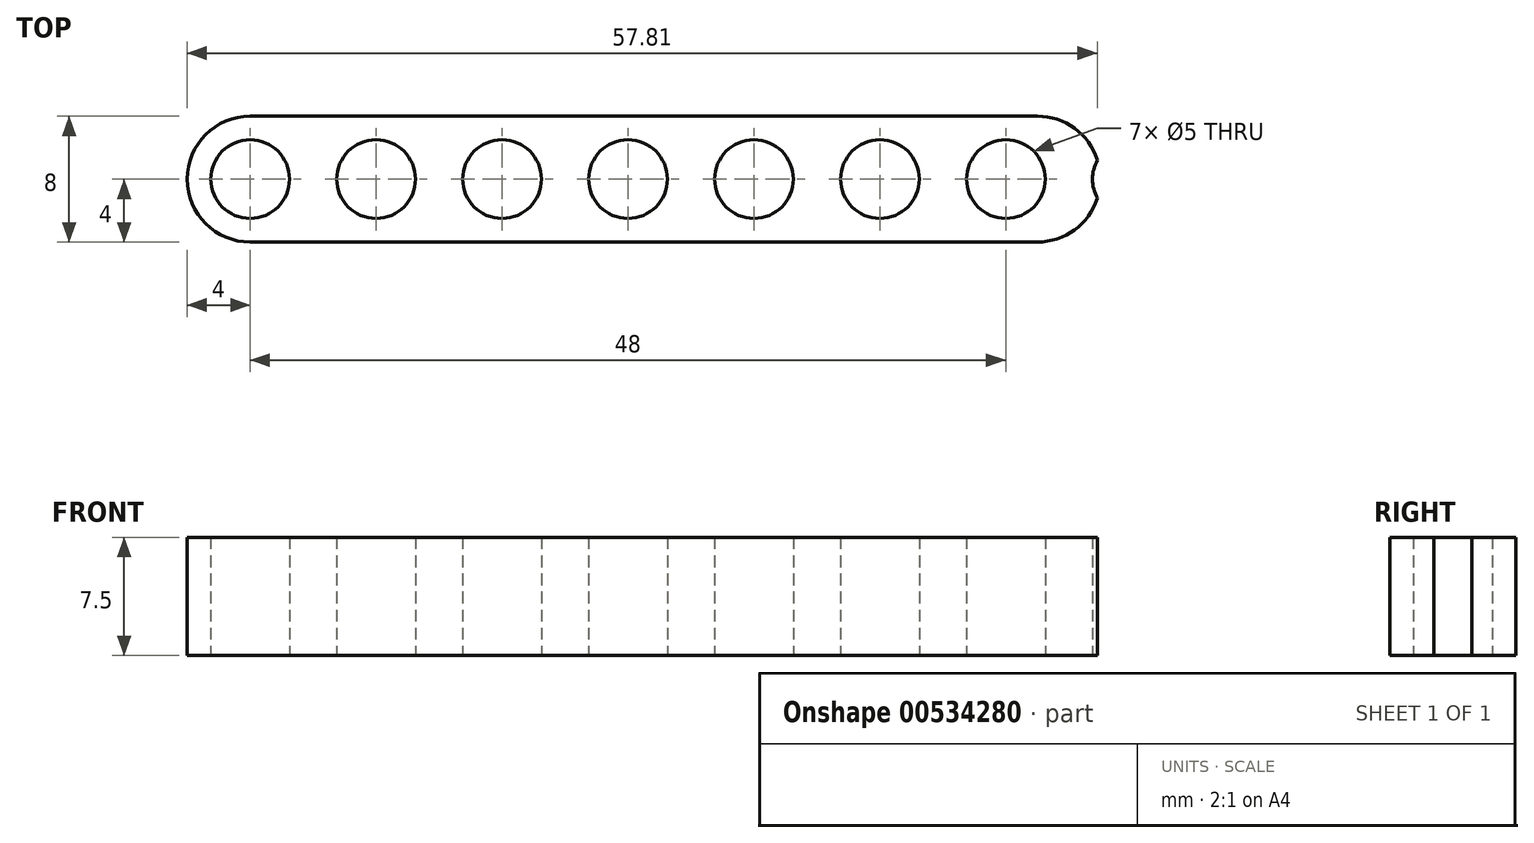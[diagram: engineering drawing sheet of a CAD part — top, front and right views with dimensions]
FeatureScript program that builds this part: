
annotation { "Feature Type Name" : "Feature", "Feature Type Description" : "" }
export const myFeature = defineFeature(function(context is Context, id is Id, definition is map)
    precondition{}
    {
        {
            var Q0;
            Q0=qCreatedBy(makeId("Top.planeOp"),FACE);
            var sketch = newSketch(context, id + "F0", { "sketchPlane" : qUnion([Q0])});
            skCircle(sketch, "E0", {"center": v(0, 0) * mm, "radius": 2.5 * mm});
            skCircle(sketch, "E1.1.0.0", {"center": v(8, 0) * mm, "radius": 2.5 * mm});
            skCircle(sketch, "E1.2.0.0", {"center": v(16, 0) * mm, "radius": 2.5 * mm});
            skCircle(sketch, "E1.3.0.0", {"center": v(24, 0) * mm, "radius": 2.5 * mm});
            skCircle(sketch, "E1.4.0.0", {"center": v(32, 0) * mm, "radius": 2.5 * mm});
            skCircle(sketch, "E1.5.0.0", {"center": v(40, 0) * mm, "radius": 2.5 * mm});
            skCircle(sketch, "E1.6.0.0", {"center": v(48, 0) * mm, "radius": 2.5 * mm});
            skArc(sketch, "E1.7.0.0", {"start": v(53.81, 1.21) * mm, "mid": v(53.5, 0) * mm, "end": v(53.81, -1.21) * mm});
            skLineSegment(sketch, "E1.direction1", {"start": v(0, 0) * mm, "end": v(8, 0) * mm, "construction": true});
            skLineSegment(sketch, "E2", {"start": v(0, 0) * mm, "end": v(50, 0) * mm, "construction": true});
            skLineSegment(sketch, "E3.bottom", {"start": v(0, -4) * mm, "end": v(50, -4) * mm});
            skLineSegment(sketch, "E3.top", {"start": v(0, 4) * mm, "end": v(50, 4) * mm});
            skArc(sketch, "E4", {"start": v(0, 4) * mm, "mid": v(-4, 0) * mm, "end": v(0, -4) * mm});
            skArc(sketch, "E5", {"start": v(50, -4) * mm, "mid": v(54, 0) * mm, "end": v(50, 4) * mm});
            skSolve(sketch);
        }
        {
            var Q0;
            Q0=makeQuery(id+"F0.imprint","IMPRINT",FACE,{"disambiguationData":[TD([[makeQuery(id+"F0.imprint","IMPRINT",EDGE,{"derivedFrom":sQuery(id+"F0.wireOp",EDGE,"E0")}),-1.0]])]});
            extrude(context, id + "F1", {"entities" : qUnion([Q0]), "endBound" : BoundingType.SYMMETRIC, "depth" : 7.5 * mm, "offsetDistance" : 25 * mm});
        }
    });
